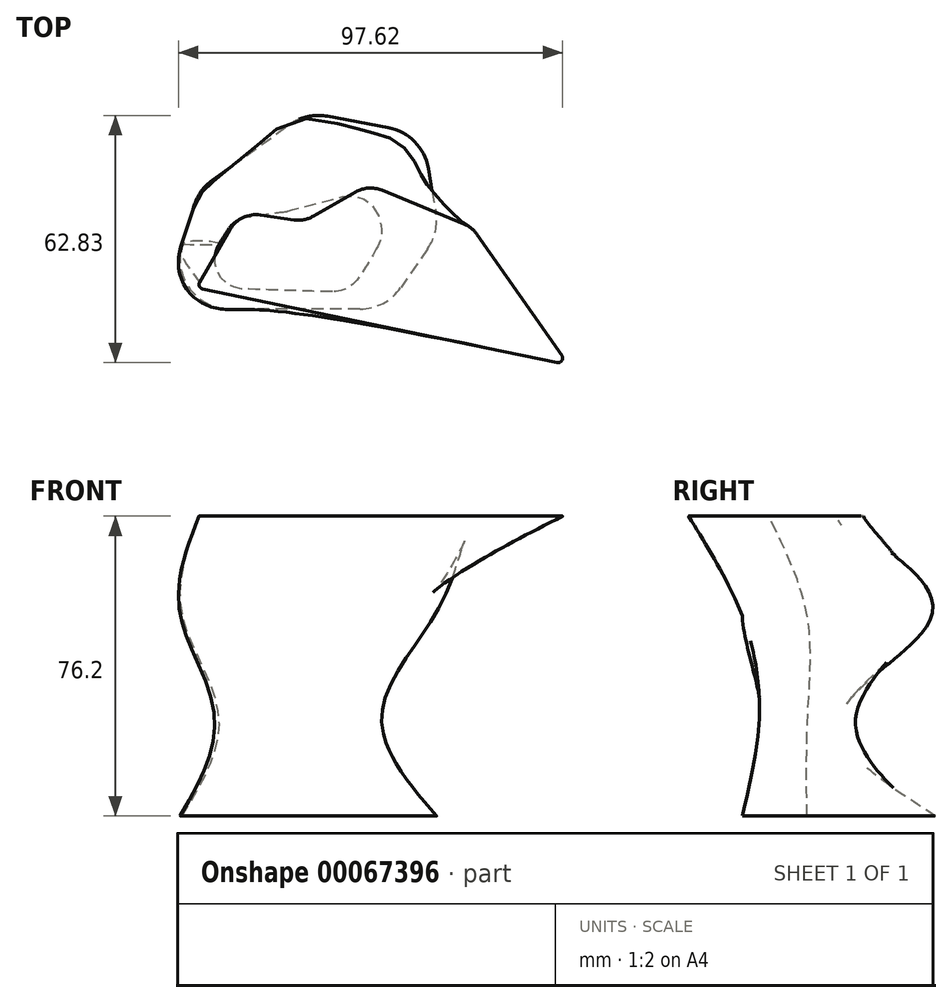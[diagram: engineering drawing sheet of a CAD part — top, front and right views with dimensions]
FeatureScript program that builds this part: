
annotation { "Feature Type Name" : "Feature", "Feature Type Description" : "" }
export const myFeature = defineFeature(function(context is Context, id is Id, definition is map)
    precondition{}
    {
        {
            var Q0;
            Q0=qCreatedBy(makeId("Top.planeOp"),FACE);
            var sketch = newSketch(context, id + "F0", { "sketchPlane" : qUnion([Q0])});
            skLineSegment(sketch, "E0", {"start": v(5.07, 16.44) * mm, "end": v(8.1, 26.24) * mm});
            skLineSegment(sketch, "E1", {"start": v(12.8, 32.8) * mm, "end": v(32.19, 46.79) * mm});
            skLineSegment(sketch, "E2", {"start": v(41.95, 48.97) * mm, "end": v(57.42, 46.08) * mm});
            skLineSegment(sketch, "E3", {"start": v(67.6, 35.74) * mm, "end": v(69.5, 24.66) * mm});
            skLineSegment(sketch, "E4", {"start": v(67.43, 15.29) * mm, "end": v(60.64, 5.47) * mm});
            skLineSegment(sketch, "E5", {"start": v(50.2, 0) * mm, "end": v(17.2, 0) * mm});
            skPoint(sketch, "E6.visualSharp", {"position": v(9.35, 30.3) * mm});
            skArc(sketch, "E6.filletArc", {"start": v(12.8, 32.8) * mm, "mid": v(9.91, 29.9) * mm, "end": v(8.1, 26.24) * mm});
            skPoint(sketch, "E7.visualSharp", {"position": v(36.6, 49.97) * mm});
            skArc(sketch, "E7.filletArc", {"start": v(41.95, 48.97) * mm, "mid": v(36.85, 48.88) * mm, "end": v(32.19, 46.79) * mm});
            skPoint(sketch, "E8.visualSharp", {"position": v(66.11, 44.46) * mm});
            skArc(sketch, "E8.filletArc", {"start": v(67.6, 35.74) * mm, "mid": v(64.14, 42.51) * mm, "end": v(57.42, 46.08) * mm});
            skPoint(sketch, "E9.visualSharp", {"position": v(70.38, 19.55) * mm});
            skArc(sketch, "E9.filletArc", {"start": v(67.43, 15.29) * mm, "mid": v(69.4, 19.77) * mm, "end": v(69.5, 24.66) * mm});
            skPoint(sketch, "E10.visualSharp", {"position": v(56.85, 0) * mm});
            skArc(sketch, "E10.filletArc", {"start": v(50.2, 0) * mm, "mid": v(56.09, 1.45) * mm, "end": v(60.64, 5.47) * mm});
            skPoint(sketch, "E11.visualSharp", {"position": v(0, 0) * mm});
            skArc(sketch, "E11.filletArc", {"start": v(5.07, 16.44) * mm, "mid": v(7, 5.16) * mm, "end": v(17.2, 0) * mm});
            skSolve(sketch);
        }
        {
            var Q0;
            Q0=qCreatedBy(makeId("Top.planeOp"),FACE);
            cPlane(context, id + "F1", {"entities" : qUnion([Q0]), "cplaneType" : CPlaneType.OFFSET, "offset" : 25.4 * mm, "width" : 152.4 * mm, "height" : 152.4 * mm});
        }
        {
            var Q0;
            Q0=qCreatedBy(id+"F1.planeOp",FACE);
            cPlane(context, id + "F2", {"entities" : qUnion([Q0]), "cplaneType" : CPlaneType.OFFSET, "offset" : 25.4 * mm, "width" : 152.4 * mm, "height" : 152.4 * mm});
        }
        {
            var Q0;
            Q0=qCreatedBy(id+"F2.planeOp",FACE);
            cPlane(context, id + "F3", {"entities" : qUnion([Q0]), "cplaneType" : CPlaneType.OFFSET, "offset" : 25.4 * mm, "width" : 152.4 * mm, "height" : 152.4 * mm});
        }
        {
            var Q0;
            Q0=qCreatedBy(id+"F1.planeOp",FACE);
            var sketch = newSketch(context, id + "F4", { "sketchPlane" : qUnion([Q0])});
            skLineSegment(sketch, "E12", {"start": v(14.42, 16.63) * mm, "end": v(16.48, 19.98) * mm});
            skLineSegment(sketch, "E13", {"start": v(21.8, 23.52) * mm, "end": v(31.02, 24.96) * mm});
            skLineSegment(sketch, "E14", {"start": v(31.68, 25.1) * mm, "end": v(45.9, 28.65) * mm});
            skLineSegment(sketch, "E15", {"start": v(55.13, 23.1) * mm, "end": v(55.54, 21.47) * mm});
            skLineSegment(sketch, "E16", {"start": v(54.77, 15.85) * mm, "end": v(50.4, 8.19) * mm});
            skLineSegment(sketch, "E17", {"start": v(43.55, 4.35) * mm, "end": v(20.69, 5.02) * mm});
            skPoint(sketch, "E18.visualSharp", {"position": v(18.32, 22.97) * mm});
            skArc(sketch, "E18.filletArc", {"start": v(21.8, 23.52) * mm, "mid": v(18.75, 22.33) * mm, "end": v(16.48, 19.98) * mm});
            skPoint(sketch, "E19.visualSharp", {"position": v(31.35, 25.02) * mm});
            skArc(sketch, "E19.filletArc", {"start": v(31.02, 24.96) * mm, "mid": v(31.35, 25.02) * mm, "end": v(31.68, 25.1) * mm});
            skPoint(sketch, "E20.visualSharp", {"position": v(53.29, 30.5) * mm});
            skArc(sketch, "E20.filletArc", {"start": v(55.13, 23.1) * mm, "mid": v(51.66, 27.8) * mm, "end": v(45.9, 28.65) * mm});
            skPoint(sketch, "E21.visualSharp", {"position": v(56.28, 18.5) * mm});
            skArc(sketch, "E21.filletArc", {"start": v(54.77, 15.85) * mm, "mid": v(55.7, 18.59) * mm, "end": v(55.54, 21.47) * mm});
            skPoint(sketch, "E22.visualSharp", {"position": v(48.13, 4.21) * mm});
            skArc(sketch, "E22.filletArc", {"start": v(43.55, 4.35) * mm, "mid": v(47.5, 5.32) * mm, "end": v(50.4, 8.19) * mm});
            skPoint(sketch, "E23.visualSharp", {"position": v(7.52, 5.41) * mm});
            skArc(sketch, "E23.filletArc", {"start": v(14.42, 16.63) * mm, "mid": v(14.2, 9.02) * mm, "end": v(20.69, 5.02) * mm});
            skSolve(sketch);
        }
        {
            var Q0;
            Q0=qCreatedBy(id+"F2.planeOp",FACE);
            var sketch = newSketch(context, id + "F5", { "sketchPlane" : qUnion([Q0])});
            skLineSegment(sketch, "E24", {"start": v(5.2, 16.51) * mm, "end": v(8.02, 25.5) * mm});
            skLineSegment(sketch, "E25", {"start": v(12.08, 31.5) * mm, "end": v(28.82, 45.23) * mm});
            skLineSegment(sketch, "E26", {"start": v(40.02, 47.72) * mm, "end": v(55.52, 43.76) * mm});
            skLineSegment(sketch, "E27", {"start": v(64.34, 35.73) * mm, "end": v(68.3, 24.63) * mm});
            skLineSegment(sketch, "E28", {"start": v(66.34, 12.52) * mm, "end": v(60.34, 4.86) * mm});
            skLineSegment(sketch, "E29", {"start": v(50.35, 0) * mm, "end": v(17.31, 0) * mm});
            skPoint(sketch, "E30.visualSharp", {"position": v(9.16, 29.1) * mm});
            skArc(sketch, "E30.filletArc", {"start": v(12.08, 31.5) * mm, "mid": v(9.62, 28.8) * mm, "end": v(8.02, 25.5) * mm});
            skPoint(sketch, "E31.visualSharp", {"position": v(33.79, 49.3) * mm});
            skArc(sketch, "E31.filletArc", {"start": v(40.02, 47.72) * mm, "mid": v(34.12, 47.81) * mm, "end": v(28.82, 45.23) * mm});
            skPoint(sketch, "E32.visualSharp", {"position": v(62.06, 42.09) * mm});
            skArc(sketch, "E32.filletArc", {"start": v(64.34, 35.73) * mm, "mid": v(60.93, 40.84) * mm, "end": v(55.52, 43.76) * mm});
            skPoint(sketch, "E33.visualSharp", {"position": v(70.67, 18.03) * mm});
            skArc(sketch, "E33.filletArc", {"start": v(66.34, 12.52) * mm, "mid": v(68.89, 18.32) * mm, "end": v(68.3, 24.63) * mm});
            skPoint(sketch, "E34.visualSharp", {"position": v(56.53, 0) * mm});
            skArc(sketch, "E34.filletArc", {"start": v(50.35, 0) * mm, "mid": v(55.9, 1.28) * mm, "end": v(60.34, 4.86) * mm});
            skPoint(sketch, "E35.visualSharp", {"position": v(0, 0) * mm});
            skArc(sketch, "E35.filletArc", {"start": v(5.2, 16.51) * mm, "mid": v(7.07, 5.19) * mm, "end": v(17.31, 0) * mm});
            skSolve(sketch);
        }
        {
            var Q0;
            Q0=qCreatedBy(id+"F3.planeOp",FACE);
            var sketch = newSketch(context, id + "F6", { "sketchPlane" : qUnion([Q0])});
            skLineSegment(sketch, "E36", {"start": v(9.51, 6.78) * mm, "end": v(17.26, 20.18) * mm});
            skLineSegment(sketch, "E37", {"start": v(24.97, 23.9) * mm, "end": v(33.48, 22.65) * mm});
            skLineSegment(sketch, "E38", {"start": v(38.39, 23.58) * mm, "end": v(49.1, 29.73) * mm});
            skLineSegment(sketch, "E39", {"start": v(55.79, 30.17) * mm, "end": v(76.62, 21.65) * mm});
            skLineSegment(sketch, "E40", {"start": v(79.98, 18.96) * mm, "end": v(101.51, -11.85) * mm});
            skLineSegment(sketch, "E41", {"start": v(100.35, -13.62) * mm, "end": v(10.27, 5.1) * mm});
            skPoint(sketch, "E42.visualSharp", {"position": v(19.85, 24.66) * mm});
            skArc(sketch, "E42.filletArc", {"start": v(24.97, 23.9) * mm, "mid": v(20.54, 23.23) * mm, "end": v(17.26, 20.18) * mm});
            skPoint(sketch, "E43.visualSharp", {"position": v(36.1, 22.26) * mm});
            skArc(sketch, "E43.filletArc", {"start": v(33.48, 22.65) * mm, "mid": v(36.01, 22.7) * mm, "end": v(38.39, 23.58) * mm});
            skPoint(sketch, "E44.visualSharp", {"position": v(52.34, 31.58) * mm});
            skArc(sketch, "E44.filletArc", {"start": v(55.79, 30.17) * mm, "mid": v(52.4, 30.72) * mm, "end": v(49.1, 29.73) * mm});
            skPoint(sketch, "E45.visualSharp", {"position": v(78.7, 20.8) * mm});
            skArc(sketch, "E45.filletArc", {"start": v(79.98, 18.96) * mm, "mid": v(78.5, 20.55) * mm, "end": v(76.62, 21.65) * mm});
            skPoint(sketch, "E46.visualSharp", {"position": v(103.15, -14.2) * mm});
            skArc(sketch, "E46.filletArc", {"start": v(100.35, -13.62) * mm, "mid": v(101.53, -13.13) * mm, "end": v(101.51, -11.85) * mm});
            skPoint(sketch, "E47.visualSharp", {"position": v(8.72, 5.41) * mm});
            skArc(sketch, "E47.filletArc", {"start": v(9.51, 6.78) * mm, "mid": v(9.46, 5.74) * mm, "end": v(10.27, 5.1) * mm});
            skSolve(sketch);
        }
        {
            var Q0;
            Q0=makeQuery(id+"F0.imprint","IMPRINT",FACE,{"disambiguationData":[TD([[makeQuery(id+"F0.imprint","IMPRINT",EDGE,{"derivedFrom":sQuery(id+"F0.wireOp",EDGE,"E0")}),-1.0]])]});
            var Q1;
            Q1=makeQuery(id+"F4.imprint","IMPRINT",FACE,{"disambiguationData":[TD([[makeQuery(id+"F4.imprint","IMPRINT",EDGE,{"derivedFrom":sQuery(id+"F4.wireOp",EDGE,"E12")}),-1.0]])]});
            var Q2;
            Q2=makeQuery(id+"F5.imprint","IMPRINT",FACE,{"disambiguationData":[TD([[makeQuery(id+"F5.imprint","IMPRINT",EDGE,{"derivedFrom":sQuery(id+"F5.wireOp",EDGE,"E24")}),-1.0]])]});
            var Q3;
            Q3=makeQuery(id+"F6.imprint","IMPRINT",FACE,{"disambiguationData":[TD([[makeQuery(id+"F6.imprint","IMPRINT",EDGE,{"derivedFrom":sQuery(id+"F6.wireOp",EDGE,"E36")}),-1.0]])]});
            loft(context, id + "F7", {"sheetProfilesArray" : [{ "sheetProfileEntities" : qUnion([Q0]) }, { "sheetProfileEntities" : qUnion([Q1]) }, { "sheetProfileEntities" : qUnion([Q2]) }, { "sheetProfileEntities" : qUnion([Q3]) }]});
        }
    });
